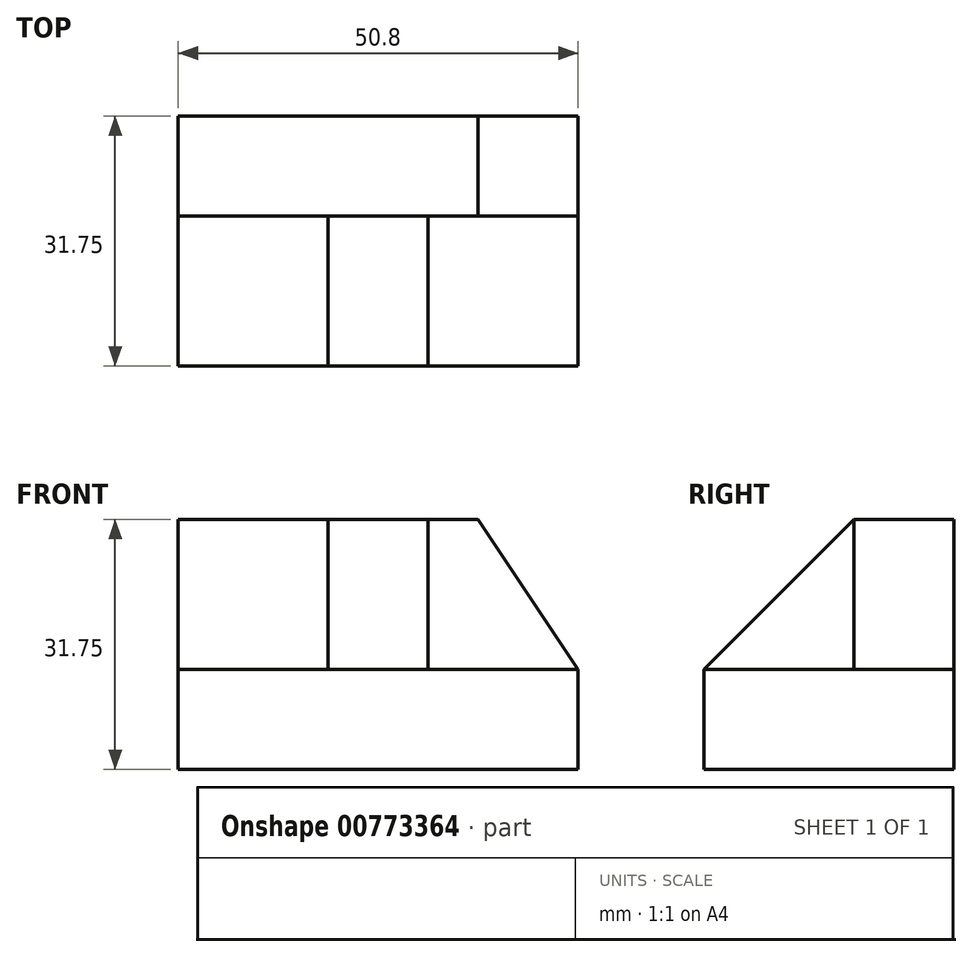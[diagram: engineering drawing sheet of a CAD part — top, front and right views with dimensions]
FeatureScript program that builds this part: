
annotation { "Feature Type Name" : "Feature", "Feature Type Description" : "" }
export const myFeature = defineFeature(function(context is Context, id is Id, definition is map)
    precondition{}
    {
        {
            var Q0;
            Q0=qCreatedBy(makeId("Front.planeOp"),FACE);
            var sketch = newSketch(context, id + "F0", { "sketchPlane" : qUnion([Q0])});
            skLineSegment(sketch, "E0", {"start": v(0, 0) * mm, "end": v(50.8, 0) * mm});
            skLineSegment(sketch, "E1", {"start": v(50.8, 0) * mm, "end": v(50.8, 31.75) * mm});
            skLineSegment(sketch, "E2", {"start": v(50.8, 31.75) * mm, "end": v(0, 31.75) * mm});
            skLineSegment(sketch, "E3", {"start": v(0, 31.75) * mm, "end": v(0, 0) * mm});
            skSolve(sketch);
        }
        {
            var Q0;
            Q0 = qSketchRegion(id + "F0", true);
            extrude(context, id + "F1", {"entities" : qUnion([Q0]), "depth" : 31.75 * mm, "offsetDistance" : 25.4 * mm});
        }
        {
            var Q0;
            Q0=makeQuery(id+"F1.opExtrude","SWEPT_FACE",FACE,{"disambiguationData":[OSD([sQuery(id+"F0.wireOp",EDGE,"E2")])]});
            var sketch = newSketch(context, id + "F2", { "sketchPlane" : qUnion([Q0])});
            skLineSegment(sketch, "E4", {"start": v(0, -31.75) * mm, "end": v(19.05, -31.75) * mm});
            skLineSegment(sketch, "E5", {"start": v(19.05, -31.75) * mm, "end": v(19.05, -12.7) * mm});
            skLineSegment(sketch, "E6", {"start": v(19.05, -12.7) * mm, "end": v(0, -12.7) * mm});
            skLineSegment(sketch, "E7", {"start": v(0, -12.7) * mm, "end": v(0, -31.75) * mm});
            skSolve(sketch);
        }
        {
            var Q0;
            Q0=makeQuery(id+"F2.imprint","IMPRINT",FACE,{"disambiguationData":[TD([[makeQuery(id+"F2.imprint","IMPRINT",EDGE,{"derivedFrom":sQuery(id+"F2.wireOp",EDGE,"E4")}),-1.0]])]});
            extrude(context, id + "F3", {"entities" : qUnion([Q0]), "operationType" : NewBodyOperationType.REMOVE, "oppositeDirection" : true, "depth" : 19.05 * mm, "offsetDistance" : 25.4 * mm});
        }
        {
            var Q0;
            Q0=makeQuery(id+"F1.opExtrude","SWEPT_FACE",FACE,{"disambiguationData":[OSD([sQuery(id+"F0.wireOp",EDGE,"E2")])]});
            var sketch = newSketch(context, id + "F4", { "sketchPlane" : qUnion([Q0])});
            skLineSegment(sketch, "E8", {"start": v(50.8, -31.75) * mm, "end": v(50.8, -12.7) * mm});
            skLineSegment(sketch, "E9", {"start": v(50.8, -12.7) * mm, "end": v(31.75, -12.7) * mm});
            skLineSegment(sketch, "E10", {"start": v(31.75, -12.7) * mm, "end": v(31.75, -31.75) * mm});
            skLineSegment(sketch, "E11", {"start": v(31.75, -31.75) * mm, "end": v(50.8, -31.75) * mm});
            skSolve(sketch);
        }
        {
            var Q0;
            Q0=makeQuery(id+"F4.imprint","IMPRINT",FACE,{"disambiguationData":[TD([[makeQuery(id+"F4.imprint","IMPRINT",EDGE,{"derivedFrom":sQuery(id+"F4.wireOp",EDGE,"E8")}),1.0]])]});
            extrude(context, id + "F5", {"entities" : qUnion([Q0]), "operationType" : NewBodyOperationType.REMOVE, "oppositeDirection" : true, "depth" : 19.05 * mm, "offsetDistance" : 25.4 * mm});
        }
        {
            var Q0;
            Q0=makeQuery(id+"F5.boolean.opBoolean","COPY",FACE,{"derivedFrom":makeQuery(id+"F5.opExtrude","SWEPT_FACE",FACE,{"disambiguationData":[OSD([sQuery(id+"F4.wireOp",EDGE,"E9")])]})});
            var sketch = newSketch(context, id + "F6", { "sketchPlane" : qUnion([Q0])});
            skLineSegment(sketch, "E12", {"start": v(31.75, 31.75) * mm, "end": v(38.1, 31.75) * mm});
            skLineSegment(sketch, "E13", {"start": v(38.1, 31.75) * mm, "end": v(50.8, 12.7) * mm});
            skSolve(sketch);
        }
        {
            var Q0;
            {var subQ0=sQuery(id+"F6.wireOp",EDGE,"E13");Q0=makeQuery(id+"F6.imprint","IMPRINT",FACE,{"disambiguationData":[TD([[makeQuery(id+"F6.imprint","IMPRINT",EDGE,{"derivedFrom":subQ0}),1.0]])]});}
            extrude(context, id + "F7", {"entities" : qUnion([Q0]), "operationType" : NewBodyOperationType.REMOVE, "oppositeDirection" : true, "depth" : 12.7 * mm, "offsetDistance" : 25.4 * mm});
        }
        {
            var Q0;
            Q0=makeQuery(id+"F5.boolean.opBoolean","COPY",FACE,{"derivedFrom":makeQuery(id+"F5.opExtrude","SWEPT_FACE",FACE,{"disambiguationData":[OSD([sQuery(id+"F4.wireOp",EDGE,"E10")])]})});
            var sketch = newSketch(context, id + "F8", { "sketchPlane" : qUnion([Q0])});
            skLineSegment(sketch, "E14", {"start": v(-12.7, 31.75) * mm, "end": v(-31.75, 12.7) * mm});
            skSolve(sketch);
        }
        {
            var Q0;
            Q0=makeQuery(id+"F8.imprint","IMPRINT",FACE,{"disambiguationData":[TD([[makeQuery(id+"F8.imprint","IMPRINT",EDGE,{"derivedFrom":sQuery(id+"F8.wireOp",EDGE,"E14")}),-1.0]])]});
            extrude(context, id + "F9", {"entities" : qUnion([Q0]), "operationType" : NewBodyOperationType.REMOVE, "oppositeDirection" : true, "depth" : 12.7 * mm, "offsetDistance" : 25.4 * mm});
        }
    });
